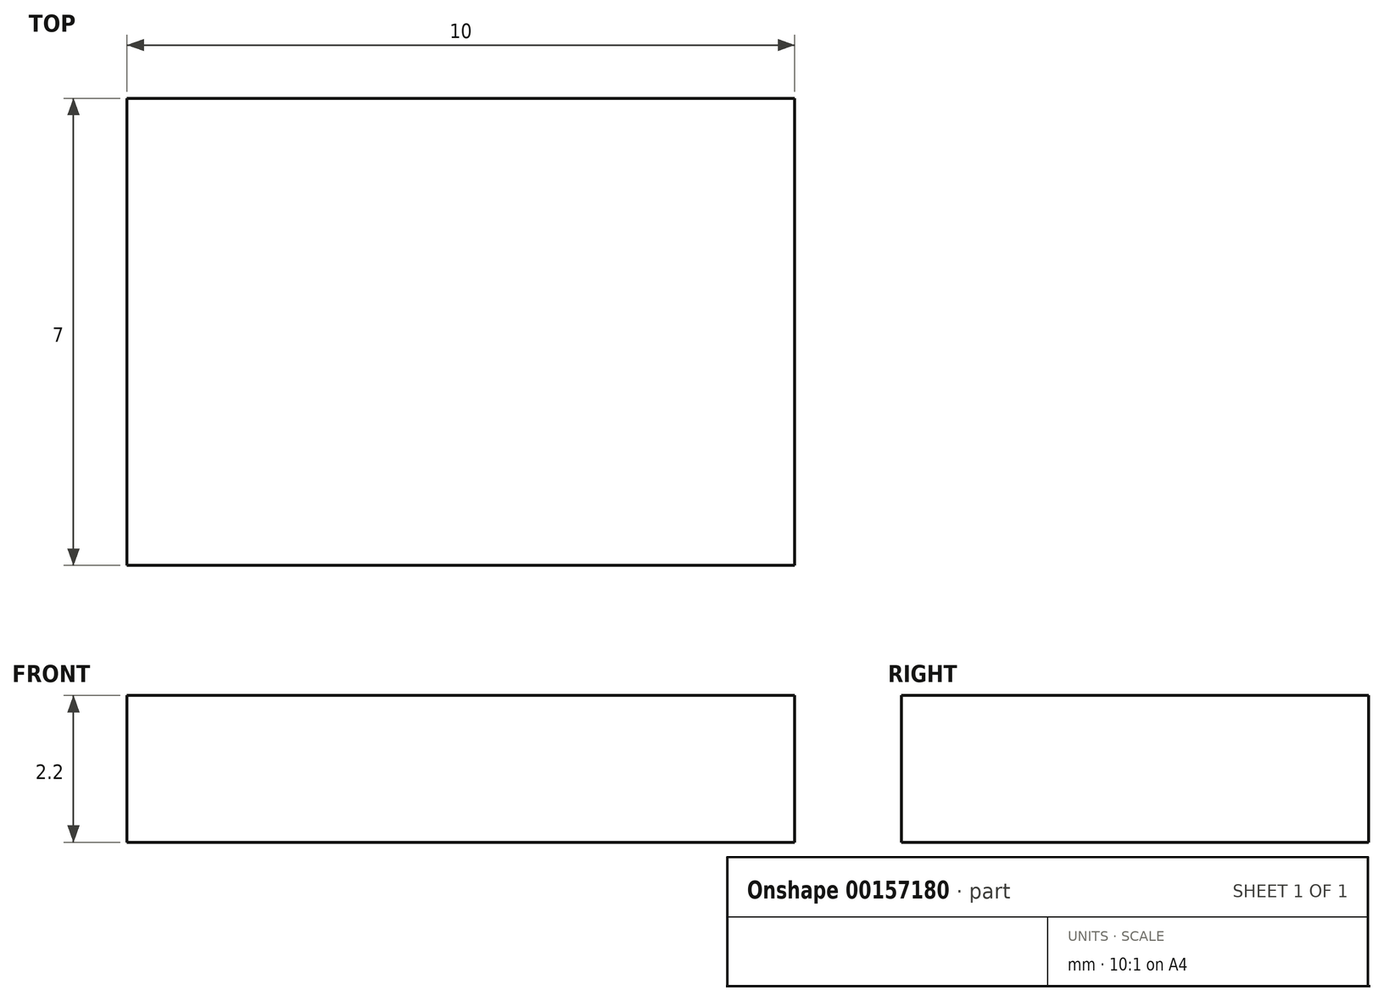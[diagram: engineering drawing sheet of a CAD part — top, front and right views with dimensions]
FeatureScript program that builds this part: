
annotation { "Feature Type Name" : "Feature", "Feature Type Description" : "" }
export const myFeature = defineFeature(function(context is Context, id is Id, definition is map)
    precondition{}
    {
        {
            var Q0;
            Q0=qCreatedBy(makeId("Top.planeOp"),FACE);
            var sketch = newSketch(context, id + "F0", { "sketchPlane" : qUnion([Q0])});
            skLineSegment(sketch, "E0.bottom", {"start": v(5, 3.5) * mm, "end": v(-5, 3.5) * mm});
            skLineSegment(sketch, "E0.top", {"start": v(5, -3.5) * mm, "end": v(-5, -3.5) * mm});
            skLineSegment(sketch, "E0.left", {"start": v(5, 3.5) * mm, "end": v(5, -3.5) * mm});
            skLineSegment(sketch, "E0.right", {"start": v(-5, 3.5) * mm, "end": v(-5, -3.5) * mm});
            skPoint(sketch, "E0.middle", {"position": v(0, 0) * mm});
            skSolve(sketch);
        }
        {
            var Q0;
            Q0=makeQuery(id+"F0.imprint","IMPRINT",FACE,{"disambiguationData":[TD([[makeQuery(id+"F0.imprint","IMPRINT",EDGE,{"derivedFrom":sQuery(id+"F0.wireOp",EDGE,"E0.bottom")}),1.0]])]});
            extrude(context, id + "F1", {"entities" : qUnion([Q0]), "endBound" : BoundingType.SYMMETRIC, "depth" : 2.2 * mm});
        }
    });
